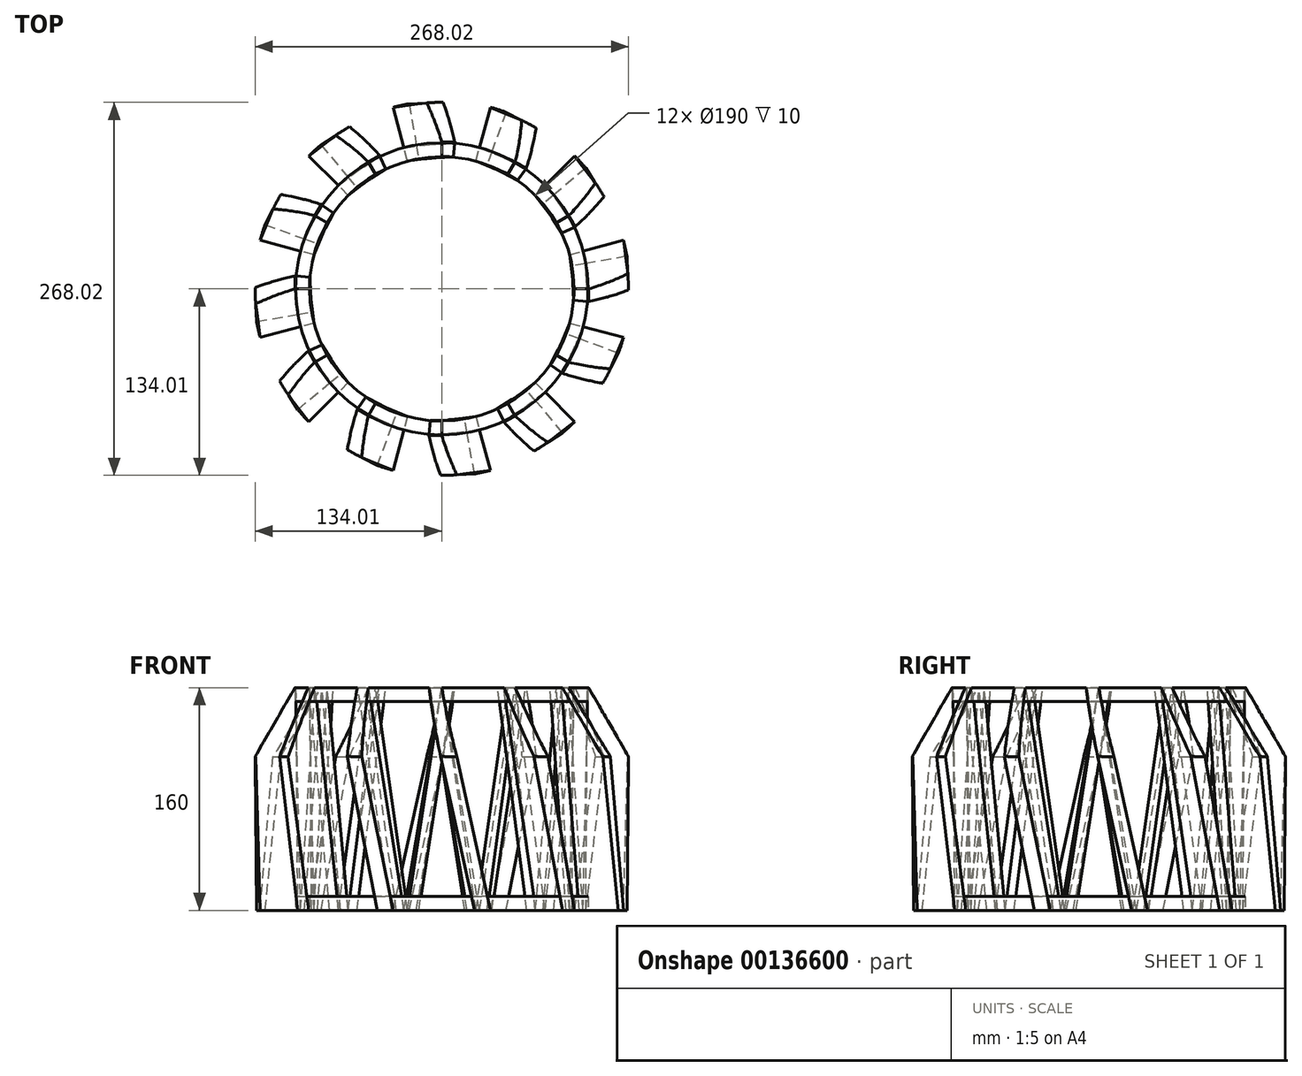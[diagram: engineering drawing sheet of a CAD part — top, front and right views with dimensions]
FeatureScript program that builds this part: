
annotation { "Feature Type Name" : "Feature", "Feature Type Description" : "" }
export const myFeature = defineFeature(function(context is Context, id is Id, definition is map)
    precondition{}
    {
        {
            var Q0;
            Q0=qCreatedBy(makeId("Top.planeOp"),FACE);
            var sketch = newSketch(context, id + "F0", { "sketchPlane" : qUnion([Q0])});
            skCircle(sketch, "E0", {"center": v(0, 0) * mm, "radius": 95 * mm});
            skCircle(sketch, "E1", {"center": v(0, 0) * mm, "radius": 135 * mm});
            skLineSegment(sketch, "E2", {"start": v(0, 0) * mm, "end": v(0, 135) * mm, "construction": true});
            skLineSegment(sketch, "E3", {"start": v(0, 0) * mm, "end": v(11.77, 134.49) * mm, "construction": true});
            skLineSegment(sketch, "E4", {"start": v(0, 135) * mm, "end": v(0, 105) * mm});
            skLineSegment(sketch, "E5", {"start": v(11.77, 134.49) * mm, "end": v(9.15, 104.6) * mm});
            skLineSegment(sketch, "E6", {"start": v(0, 95) * mm, "end": v(0, 105) * mm});
            skLineSegment(sketch, "E7", {"start": v(8.28, 94.64) * mm, "end": v(9.15, 104.6) * mm});
            skCircle(sketch, "E8.converted", {"center": v(0, 0) * mm, "radius": 105 * mm});
            skSolve(sketch);
        }
        {
            var Q0;
            Q0=makeQuery(id+"F0.imprint","IMPRINT",FACE,{"disambiguationData":[TD([[makeQuery(id+"F0.imprint","IMPRINT",EDGE,{"derivedFrom":sQuery(id+"F0.wireOp",EDGE,"E0")}),-1.0]])]});
            extrude(context, id + "F1", {"entities" : qUnion([Q0]), "depth" : 10 * mm});
        }
        {
            var Q0;
            Q0=makeQuery(id+"F1.opExtrude","SWEPT_BODY",BODY,{"disambiguationData":[OSD([sQuery(id+"F0.wireOp",EDGE,"E0"),sQuery(id+"F0.wireOp",EDGE,"auEbFCTJ-X7dO-mgTi-bPjS-Xb70D8OlHXF6")])]});
            transform(context, id + "F2", {"entities" : qUnion([Q0]), "transformType" : TransformType.TRANSLATION_3D, "dx" : 0 * mm, "dy" : 0 * mm, "dz" : -160 * mm, "makeCopy" : false});
        }
        {
            var Q0;
            Q0=makeQuery(id+"F0.imprint","IMPRINT",FACE,{"disambiguationData":[TD([[makeQuery(id+"F0.imprint","IMPRINT",EDGE,{"derivedFrom":sQuery(id+"F0.wireOp",EDGE,"E0")}),-1.0]])]});
            extrude(context, id + "F3", {"entities" : qUnion([Q0]), "oppositeDirection" : true, "depth" : 10 * mm});
        }
        {
            var Q0;
            Q0=makeQuery(id+"F1.opExtrude","CAP_FACE",FACE,{"disambiguationData":[OSD([sQuery(id+"F0.wireOp",EDGE,"E0"),sQuery(id+"F0.wireOp",EDGE,"E8.converted")])],"isStart":true});
            var sketch = newSketch(context, id + "F4", { "sketchPlane" : qUnion([Q0])});
            skCircle(sketch, "E9", {"center": v(0, 0) * mm, "radius": 135 * mm});
            skLineSegment(sketch, "E10", {"start": v(0, 0) * mm, "end": v(0, -135) * mm, "construction": true});
            skLineSegment(sketch, "E11", {"start": v(0, 0) * mm, "end": v(-34.94, -130.4) * mm, "construction": true});
            skLineSegment(sketch, "E12", {"start": v(0, 0) * mm, "end": v(-23.44, -132.95) * mm, "construction": true});
            skLineSegment(sketch, "E13", {"start": v(-24.59, -91.76) * mm, "end": v(-34.94, -130.4) * mm});
            skLineSegment(sketch, "E14", {"start": v(-23.44, -132.95) * mm, "end": v(-16.5, -93.56) * mm});
            skSolve(sketch);
        }
        {
            var Q0;
            {var subQ0=sQuery(id+"F4.wireOp",EDGE,"E13");var subQ1=makeQuery(id+"F1.opExtrude","CAP_EDGE",EDGE,{"disambiguationData":[OSD([sQuery(id+"F0.wireOp",EDGE,"E0")])],"isStart":true});var subQ2=makeQuery(id+"F4.imprint","INTERSECT",VERTEX,{"derivedFrom":[subQ1,subQ0]});Q0=makeQuery(id+"F4.imprint","IMPRINT",FACE,{"disambiguationData":[TD([[makeQuery(id+"F4.imprint","IMPRINT",EDGE,{"disambiguationData":[TD([[subQ2,-1.0]])],"derivedFrom":subQ0}),1.0]])]});}
            var Q1;
            {var subQ0=sQuery(id+"F0.wireOp",EDGE,"E6");Q1=makeQuery(id+"F0.imprint","IMPRINT",FACE,{"disambiguationData":[TD([[makeQuery(id+"F0.imprint","IMPRINT",EDGE,{"derivedFrom":subQ0}),-1.0]])]});}
            loft(context, id + "F5", {"sheetProfilesArray" : [{ "sheetProfileEntities" : qUnion([Q0]) }, { "sheetProfileEntities" : qUnion([Q1]) }]});
        }
        {
            var Q0;
            {var subQ0=sQuery(id+"F4.wireOp",EDGE,"E13");var subQ1=sQuery(id+"F4.wireOp",EDGE,"E9");var subQ2=makeQuery(id+"F4.imprint","INTERSECT",VERTEX,{"derivedFrom":[subQ1,subQ0]});Q0=makeQuery(id+"F4.imprint","IMPRINT",FACE,{"disambiguationData":[TD([[makeQuery(id+"F4.imprint","IMPRINT",EDGE,{"disambiguationData":[TD([[subQ2,-1.0]])],"derivedFrom":subQ1}),1.0]])]});}
            var Q1;
            {var subQ0=sQuery(id+"F0.wireOp",EDGE,"E4");Q1=makeQuery(id+"F0.imprint","IMPRINT",FACE,{"disambiguationData":[TD([[makeQuery(id+"F0.imprint","IMPRINT",EDGE,{"derivedFrom":subQ0}),1.0]])]});}
            loft(context, id + "F6", {"sheetProfilesArray" : [{ "sheetProfileEntities" : qUnion([Q0]) }, { "sheetProfileEntities" : qUnion([Q1]) }]});
        }
        {
            var Q0;
            Q0=makeQuery(id+"F6.opLoft","MID_CAP_EDGE",EDGE,{"disambiguationData":[OSD([sQuery(id+"F0.wireOp",EDGE,"E1"),sQuery(id+"F0.wireOp",EDGE,"E4"),sQuery(id+"F0.wireOp",EDGE,"E5")])],"capPos":1.0});
            chamfer(context, id + "F7", {"entities" : qUnion([Q0]), "chamferType" : ChamferType.TWO_OFFSETS, "width1" : 30 * mm, "oppositeDirection" : false, "width2" : 50 * mm, "tangentPropagation" : true});
        }
        {
            var Q0;
            {var subQ0=sQuery(id+"F4.wireOp",EDGE,"E13");var subQ1=sQuery(id+"F4.wireOp",EDGE,"E9");var subQ2=makeQuery(id+"F4.imprint","INTERSECT",VERTEX,{"derivedFrom":[subQ1,subQ0]});var subQ9=sQuery(id+"F0.wireOp",EDGE,"E4");Q0=makeQuery(id+"F6.opLoft","SWEPT_BODY",BODY,{"disambiguationData":[OSD([makeQuery(id+"F0.imprint","IMPRINT",FACE,{"disambiguationData":[TD([[makeQuery(id+"F0.imprint","IMPRINT",EDGE,{"derivedFrom":subQ9}),1.0]])]}),makeQuery(id+"F4.imprint","IMPRINT",FACE,{"disambiguationData":[TD([[makeQuery(id+"F4.imprint","IMPRINT",EDGE,{"disambiguationData":[TD([[subQ2,-1.0]])],"derivedFrom":subQ1}),1.0]])]})])]});}
            var Q1;
            {var subQ0=sQuery(id+"F4.wireOp",EDGE,"E13");var subQ1=sQuery(id+"F0.wireOp",EDGE,"E0");var subQ2=makeQuery(id+"F1.opExtrude","CAP_EDGE",EDGE,{"disambiguationData":[OSD([subQ1])],"isStart":true});var subQ3=makeQuery(id+"F4.imprint","INTERSECT",VERTEX,{"derivedFrom":[subQ2,subQ0]});var subQ10=sQuery(id+"F0.wireOp",EDGE,"E6");Q1=makeQuery(id+"F5.opLoft","SWEPT_BODY",BODY,{"disambiguationData":[OSD([makeQuery(id+"F0.imprint","IMPRINT",FACE,{"disambiguationData":[TD([[makeQuery(id+"F0.imprint","IMPRINT",EDGE,{"derivedFrom":subQ10}),-1.0]])]}),makeQuery(id+"F4.imprint","IMPRINT",FACE,{"disambiguationData":[TD([[makeQuery(id+"F4.imprint","IMPRINT",EDGE,{"disambiguationData":[TD([[subQ3,-1.0]])],"derivedFrom":subQ0}),1.0]])]})])]});}
            var Q2;
            Q2=makeQuery(id+"F3.opExtrude","SWEPT_FACE",FACE,{"disambiguationData":[OSD([sQuery(id+"F0.wireOp",EDGE,"E8.converted")])]});
            circularPattern(context, id + "F8", {"entities" : qUnion([Q0, Q1]), "axis" : qUnion([Q2]), "angle" : 30 * degree, "instanceCount" : 12});
        }
    });
